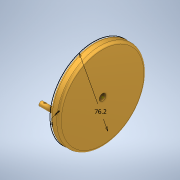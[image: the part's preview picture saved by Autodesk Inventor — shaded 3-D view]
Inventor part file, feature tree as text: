
AUTODESK INVENTOR PART (.ipt)
format: ipt  version: 2022 (Build 260153070, 153G)  size: 149,504 bytes
history: native  units: mm
features: extrude x4, sketch x4, fillet x1
ambient origin geometry x8: Origin, YZ Plane, XZ Plane, XY Plane, X Axis, Y Axis, Z Axis, Center Point
bodies: Solid1 (feature_tree)
feature tree (9):
  extrude  "Extrusion1"  Depth=8.0mm TaperAngle=0.0deg
  extrude  "Extrusion2"  TaperAngle=0.0deg  [1 undecoded]
  fillet  "Fillet1"  Radius=2.0mm
  sketch  "Sketch4"  dims[d3=6.0mm d4=0.0mm d5=0.0mm d9=2.0mm]
  sketch  "Sketch7"  dims[d14=4.0mm d15=14.0mm d16=0.0mm]
  extrude  "Extrusion5"  Depth=14.0mm TaperAngle=0.0deg
  extrude  "Extrusion6"  Depth=2.0mm
  sketch  "Sketch2"  dims[d0=76.2mm d1=8.0mm d2=0.0mm]
  sketch  "Sketch8"  dims[d17=2.0mm d18=3.0mm d19=14.0mm d20=0.0mm]
note: 1 required parameter value undecoded (feature->parameter linkage not recoverable at this tier; creation-order binding heuristic only, values carry confidence <= 0.55)
